# Revit family: ARJO_Symbliss_Standard Tub
name_source: partatom
category: Equipement spécialisé
revit_build: Autodesk Revit 2018 (Build: 20170223_1515(x64)
units: mm (PartAtom-declared; Revit-internal decimal feet)

## family parameters
Cote de connecteur circulaire = Utiliser le diamètre
Couper avec des vides une fois chargée = Non
Hôte = Face
Numéro OmniClass = 23.45.05.00
Partagée = Non
Point de calcul de pièce = Non
Titre OmniClass = Sanitary Equipment
Type d'élément = Normal

## types (1)
- SYMBLISS (Standard)
    BIMObjectName = Symbliss (Standard)
    Bath material = ARJO_White
    Category = Medical
    Color = White
    Commentaires du type = https://www.arjo.com
    Description = Height adjustable bath tub
    Elévation par défaut = 1219.2 mm  [stored 4 ft]
    Fabricant = Arjo
    Filling time = TBD
    High-Low Position = Yes
    IP Rate for Device = IPX4
    IfcExportAs = Sanitary Terminal
    Length = 2107 mm
    Manufacturer = Arjo
    ManufacturerURL = https://www.arjo.com
    Material = Acrylic, RTM, multiple
    Max Water temperature = 55-80 C
    MaxHeight = 1180
    Min Water temperature = 5 C
    Modèle = Standard Tub Keystone
    NominalHeight = 800 mm
    NominalLength = 2110 mm
    NominalWidth = 910 mm
    Power supply = AC
    Revision = 0
    SafeWorkingLoad (SWL) = 472 kg (1040 lbs.)
    Tap material = ARJO_Silver
    Uniclass 2015 Code = Pr_40_20_06_36
    Uniclass 2015 Name = Health care general baths
    Version = 0
    WarrantyStartDate (default) = Installation date
    Water Inlet Connection = G 3/4" male
    Water consumption = 243 l (fill level mid)
    Width = 904 mm

note: [stored X ft] marks values corroborated as IEEE doubles in the binary element streams (Revit-internal decimal feet)

## geometry (parser evidence)
native form markers: Sweep x4
no freeform markers — native parametric forms only
